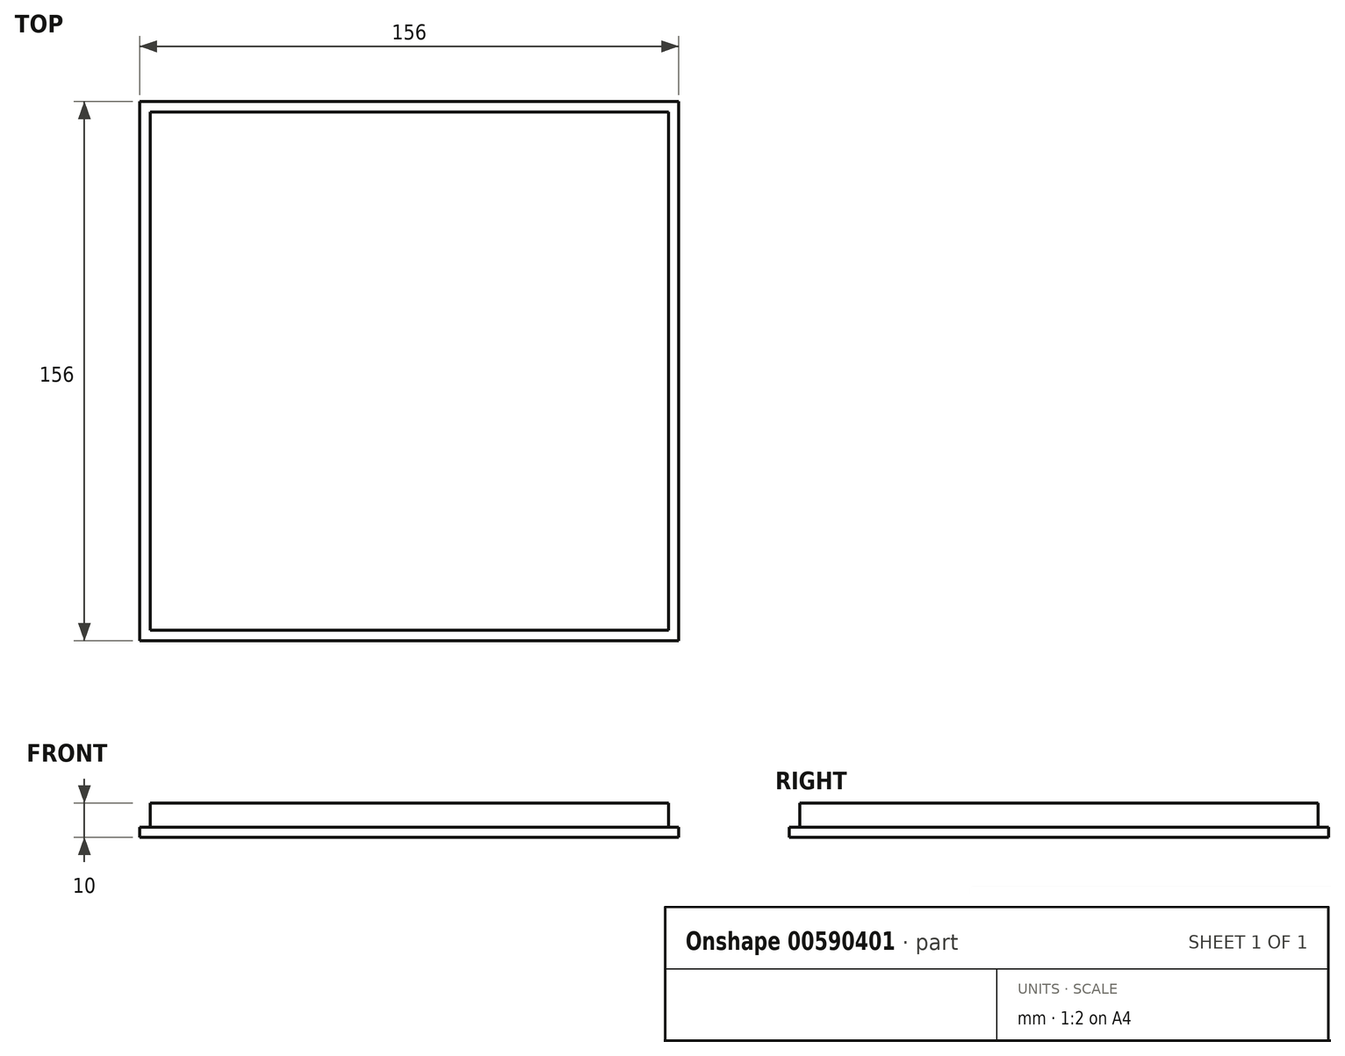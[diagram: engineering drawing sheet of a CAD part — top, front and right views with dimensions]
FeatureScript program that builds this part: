
annotation { "Feature Type Name" : "Feature", "Feature Type Description" : "" }
export const myFeature = defineFeature(function(context is Context, id is Id, definition is map)
    precondition{}
    {
        {
            var Q0;
            Q0=qCreatedBy(makeId("Top.planeOp"),FACE);
            var sketch = newSketch(context, id + "F0", { "sketchPlane" : qUnion([Q0])});
            skLineSegment(sketch, "E0.bottom", {"start": v(74.63, -73.33) * mm, "end": v(-75.37, -73.33) * mm});
            skLineSegment(sketch, "E0.top", {"start": v(74.63, 76.67) * mm, "end": v(-75.37, 76.67) * mm});
            skLineSegment(sketch, "E0.left", {"start": v(74.63, -73.33) * mm, "end": v(74.63, 76.67) * mm});
            skLineSegment(sketch, "E0.right", {"start": v(-75.37, -73.33) * mm, "end": v(-75.37, 76.67) * mm});
            skPoint(sketch, "E0.middle", {"position": v(-0.37, 1.67) * mm});
            skSolve(sketch);
        }
        {
            var Q0;
            Q0 = qSketchRegion(id + "F0", true);
            var sketch = newSketch(context, id + "F1", { "sketchPlane" : qUnion([Q0])});
            skLineSegment(sketch, "E1.0", {"start": v(-78.37, -76.33) * mm, "end": v(-78.37, 79.67) * mm});
            skLineSegment(sketch, "E1.1", {"start": v(77.63, -76.33) * mm, "end": v(-78.37, -76.33) * mm});
            skLineSegment(sketch, "E1.2", {"start": v(77.63, -76.33) * mm, "end": v(77.63, 79.67) * mm});
            skLineSegment(sketch, "E1.3", {"start": v(77.63, 79.67) * mm, "end": v(-78.37, 79.67) * mm});
            skSolve(sketch);
        }
        {
            var Q0;
            Q0=makeQuery(id+"F0.imprint","IMPRINT",FACE,{"disambiguationData":[TD([[makeQuery(id+"F0.imprint","IMPRINT",EDGE,{"derivedFrom":sQuery(id+"F0.wireOp",EDGE,"E0.bottom")}),-1.0]])]});
            extrude(context, id + "F2", {"entities" : qUnion([Q0]), "depth" : 10 * mm, "offsetDistance" : 25 * mm});
        }
        {
            var Q0;
            Q0=makeQuery(id+"F1.imprint","IMPRINT",FACE,{"disambiguationData":[TD([[makeQuery(id+"F1.imprint","IMPRINT",EDGE,{"derivedFrom":sQuery(id+"F1.wireOp",EDGE,"E1.0")}),-1.0]])]});
            extrude(context, id + "F3", {"entities" : qUnion([Q0]), "operationType" : NewBodyOperationType.ADD, "depth" : 3 * mm, "offsetDistance" : 25 * mm});
        }
    });
